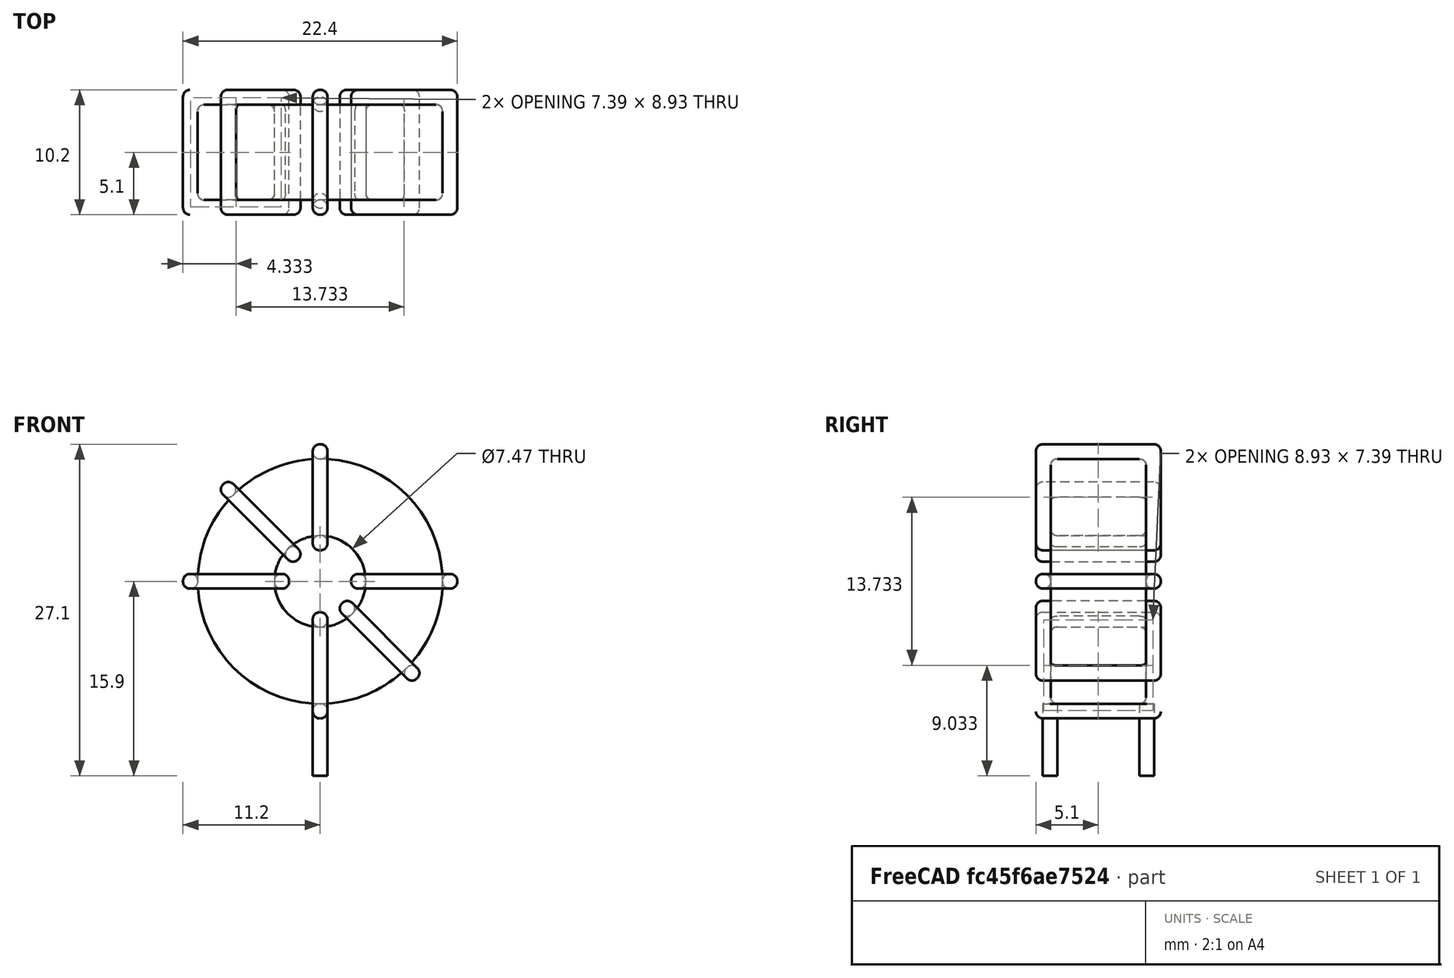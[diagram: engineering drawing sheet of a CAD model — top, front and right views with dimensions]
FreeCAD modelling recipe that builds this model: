
FCSTD DOCUMENT  (FreeCAD 0.16R6703 (Git))
Label: L_Toroid_Vertical_L22.4mm_W10.2mm_P7.90mm_Vishay_TJ4
License: All rights reserved
LicenseURL: http://en.wikipedia.org/wiki/All_rights_reserved
objects: Sketcher::SketchObject×6, PartDesign::Pad×6, PartDesign::Fillet×5, Spreadsheet::Sheet×1
note: 23 computed .brp shape members not serialized (recipe doc carries the construction recipe); baked Part::Feature solids carry a one-line shape summary decoded from their .brp

FEATURE [Spreadsheet::Sheet] Spreadsheet  label="dimensions"
  cells = A1=Wx; B1(Wx)=22.4; C1(WW)=7.466666666666666; D1=22.4; A2=Wy; B2(Wy)=10.2; D2=10.2; A3=RM; B3(RMx)=7.9; C3(RMy)=0; A4=d_wire; B4(d_wire)=1.2; A5=H; B5(H)=22.4; A6=offsetx; B6(offsetx)=11.2
FEATURE [Sketcher::SketchObject] Sketch
  Placement = pos=(0,-3.95,0) rot=(1,0,0;1.5708rad)
  expr: Placement.Base.y = -Spreadsheet.RMx / 2
  expr: Constraints[0] = Spreadsheet.Wx / 2 - Spreadsheet.d_wire
  expr: Constraints[4] = Spreadsheet.WW / 2
  expr: Constraints[2] = Spreadsheet.Wx / 2 + Spreadsheet.d_wire + 0.5
  sketch-geometry (2):
    g0: Circle CenterX=0 CenterY=12.9 CenterZ=0 NormalX=0 NormalY=0 NormalZ=1 Radius=10
    g1: Circle CenterX=0 CenterY=12.9 CenterZ=0 NormalX=0 NormalY=0 NormalZ=1 Radius=3.73333
  constraints (5):
    c: Radius(g0) = 10
    c: DistanceX(g-1,g0) = 0
    c: DistanceY(g-1,g0) = 12.9
    c: Coincident(g1,g0)
    c: Radius(g1) = 3.73333
FEATURE [PartDesign::Pad] Pad
  Length = 7.8
  Length2 = 100
  Midplane = true
  Placement = pos=(0,-3.95,0) rot=(1,0,0;1.5708rad)
  Sketch = -> Sketch
  Type = 0
  expr: Length = Spreadsheet.Wy - 2 * Spreadsheet.d_wire
FEATURE [Sketcher::SketchObject] Sketch001
  Placement = pos=(0,0,1.7) rot=(0,0,1;0rad)
  expr: Placement.Base.z = 0.5 + Spreadsheet.d_wire
  expr: Constraints[4] = Spreadsheet.RMy
  expr: Constraints[2] = -Spreadsheet.RMx
  expr: Constraints[1] = Spreadsheet.d_wire / 2
  sketch-geometry (2):
    g0: Circle CenterX=0 CenterY=0 CenterZ=0 NormalX=0 NormalY=0 NormalZ=1 Radius=0.6
    g1: Circle CenterX=0 CenterY=-7.9 CenterZ=0 NormalX=0 NormalY=0 NormalZ=1 Radius=0.6
  constraints (5):
    c: Equal(g0,g1)
    c: Radius(g0) = 0.6
    c: DistanceY(g-1,g1) = -7.9
    c: Coincident(g0,g-1)
    c: DistanceX(g-1,g1) = 0
FEATURE [PartDesign::Pad] Pad001
  Length = 1.2
  Length2 = 4.7
  Placement = pos=(0,0,1.7) rot=(0,0,1;0rad)
  Reversed = true
  Sketch = -> Sketch001
  Type = 4
  expr: Length2 = 3.5 + Spreadsheet.d_wire
  expr: Length = Spreadsheet.d_wire
FEATURE [PartDesign::Fillet] Fillet
  Base = -> Pad [Edge6,Edge3,Edge2]
  Placement = pos=(0,-3.95,0) rot=(1,0,0;1.5708rad)
  Radius = 0.5
FEATURE [Sketcher::SketchObject] Sketch003
  Placement = pos=(0,1.15,12.9) rot=(1,0,0;3.14159rad)
  expr: Constraints[18] = Spreadsheet.d_wire
  expr: Constraints[16] = Spreadsheet.d_wire
  expr: Constraints[19] = Spreadsheet.d_wire
  expr: Constraints[17] = Spreadsheet.d_wire
  expr: Placement.Base.y = -1 * (Spreadsheet.RMx - Spreadsheet.Wy) / 2
  expr: Constraints[21] = (Spreadsheet.Wx - Spreadsheet.WW) / 2 - Spreadsheet.d_wire
  expr: Constraints[22] = Spreadsheet.Wx / 2 - Spreadsheet.d_wire
  expr: Constraints[43] = Spreadsheet.d_wire
  expr: Constraints[48] = Spreadsheet.Wx - Spreadsheet.d_wire * 2
  expr: Constraints[49] = Spreadsheet.Wy
  expr: Placement.Base.z = Spreadsheet.Wx / 2 + Spreadsheet.d_wire + 0.5
  sketch-geometry (16):
    g0: LineSegment StartX=-2.53333 StartY=0 StartZ=0 EndX=-11.2 EndY=0 EndZ=0
    g1: LineSegment StartX=-11.2 StartY=0 StartZ=0 EndX=-11.2 EndY=10.2 EndZ=0
    g2: LineSegment StartX=-11.2 StartY=10.2 StartZ=0 EndX=-2.53333 EndY=10.2 EndZ=0
    g3: LineSegment StartX=-2.53333 StartY=10.2 StartZ=0 EndX=-2.53333 EndY=0 EndZ=0
    g4: LineSegment StartX=-10 StartY=9 StartZ=0 EndX=-3.73333 EndY=9 EndZ=0
    g5: LineSegment StartX=-3.73333 StartY=9 StartZ=0 EndX=-3.73333 EndY=1.2 EndZ=0
    g6: LineSegment StartX=-3.73333 StartY=1.2 StartZ=0 EndX=-10 EndY=1.2 EndZ=0
    g7: LineSegment StartX=-10 StartY=1.2 StartZ=0 EndX=-10 EndY=9 EndZ=0
    g8: LineSegment StartX=2.53333 StartY=10.2 StartZ=0 EndX=11.2 EndY=10.2 EndZ=0
    g9: LineSegment StartX=11.2 StartY=10.2 StartZ=0 EndX=11.2 EndY=0 EndZ=0
    g10: LineSegment StartX=11.2 StartY=0 StartZ=0 EndX=2.53333 EndY=0 EndZ=0
    g11: LineSegment StartX=2.53333 StartY=0 StartZ=0 EndX=2.53333 EndY=10.2 EndZ=0
    g12: LineSegment StartX=3.73333 StartY=9 StartZ=0 EndX=10 EndY=9 EndZ=0
    g13: LineSegment StartX=10 StartY=9 StartZ=0 EndX=10 EndY=1.2 EndZ=0
    g14: LineSegment StartX=10 StartY=1.2 StartZ=0 EndX=3.73333 EndY=1.2 EndZ=0
    g15: LineSegment StartX=3.73333 StartY=1.2 StartZ=0 EndX=3.73333 EndY=9 EndZ=0
  constraints (50):
    c: Horizontal(g0)
    c: Coincident(g1,g0)
    c: Vertical(g1)
    c: Coincident(g2,g1)
    c: Horizontal(g2)
    c: Coincident(g3,g2)
    c: Coincident(g3,g0)
    c: Vertical(g3)
    c: Coincident(g4,g5)
    c: Coincident(g5,g6)
    c: Coincident(g6,g7)
    c: Coincident(g7,g4)
    c: Horizontal(g4)
    c: Horizontal(g6)
    c: Vertical(g5)
    c: Vertical(g7)
    c: DistanceX(g1,g4) = 1.2
    c: DistanceY(g4,g1) = 1.2
    c: DistanceX(g5,g0) = 1.2
    c: DistanceY(g0,g5) = 1.2
    c: DistanceY(g-1,g0) = 0
    c: DistanceX(g6,g6) = 6.26667
    c: DistanceX(g6,g-1) = 10
    c: Coincident(g8,g9)
    c: Coincident(g9,g10)
    c: Coincident(g10,g11)
    c: Coincident(g11,g8)
    c: Horizontal(g8)
    c: Horizontal(g10)
    c: Vertical(g9)
    c: Vertical(g11)
    c: Coincident(g12,g13)
    c: Coincident(g13,g14)
    c: Coincident(g14,g15)
    c: Coincident(g15,g12)
    c: Horizontal(g12)
    c: Horizontal(g14)
    c: Vertical(g13)
    c: Vertical(g15)
    c: DistanceY(g8,g2) = 0
    c: DistanceY(g10,g0) = 0
    c: DistanceY(g14,g5) = 0
    c: DistanceY(g12,g4) = 0
    c: DistanceX(g8,g12) = 1.2
    c: Equal(g8,g2)
    c: Equal(g12,g4)
    c: Equal(g9,g1)
    c: Equal(g13,g7)
    c: DistanceX(g4,g12) = 20
    c: DistanceY(g0,g1) = 10.2
FEATURE [PartDesign::Pad] Pad002
  Length = 1.2
  Length2 = 100
  Midplane = true
  Placement = pos=(0,1.15,12.9) rot=(1,0,0;3.14159rad)
  Sketch = -> Sketch003
  Type = 0
  expr: Length = Spreadsheet.d_wire
FEATURE [PartDesign::Fillet] Fillet001
  Base = -> Pad002 [Edge38,Edge41,Edge42,Edge43,Edge29,Edge32,Edge33,Edge34,Edge25,Edge35,Edge36,Edge13,Edge14,Edge15,Edge16,Edge17,Edge18,Edge19,Edge1,Edge2,Edge3,Edge4,Edge5,Edge6,Edge7,Edge37,Edge39,Edge40,Edge20,Edge23,Edge24,Edge21,Edge22,Edge8,Edge9,Edge10,Edge11,Edge12,Edge26,Edge27,+8 more]
  Placement = pos=(0,1.15,12.9) rot=(1,0,0;3.14159rad)
  Radius = 0.564
  expr: Radius = Spreadsheet.d_wire * 0.47
FEATURE [Sketcher::SketchObject] Sketch004
  Placement = pos=(0,1.15,12.9) rot=(0.92388,0,0.382683;3.14159rad)
  expr: Constraints[18] = Spreadsheet.d_wire
  expr: Constraints[16] = Spreadsheet.d_wire
  expr: Constraints[19] = Spreadsheet.d_wire
  expr: Constraints[17] = Spreadsheet.d_wire
  expr: Placement.Base.y = -1 * (Spreadsheet.RMx - Spreadsheet.Wy) / 2
  expr: Constraints[21] = (Spreadsheet.Wx - Spreadsheet.WW) / 2 - Spreadsheet.d_wire
  expr: Constraints[22] = Spreadsheet.Wx / 2 - Spreadsheet.d_wire
  expr: Constraints[43] = Spreadsheet.d_wire
  expr: Constraints[48] = Spreadsheet.Wx - 2 * Spreadsheet.d_wire
  expr: Constraints[49] = Spreadsheet.Wy
  expr: Placement.Base.z = Spreadsheet.Wx / 2 + Spreadsheet.d_wire + 0.5
  sketch-geometry (16):
    g0: LineSegment StartX=-2.53333 StartY=0 StartZ=0 EndX=-11.2 EndY=0 EndZ=0
    g1: LineSegment StartX=-11.2 StartY=0 StartZ=0 EndX=-11.2 EndY=10.2 EndZ=0
    g2: LineSegment StartX=-11.2 StartY=10.2 StartZ=0 EndX=-2.53333 EndY=10.2 EndZ=0
    g3: LineSegment StartX=-2.53333 StartY=10.2 StartZ=0 EndX=-2.53333 EndY=0 EndZ=0
    g4: LineSegment StartX=-10 StartY=9 StartZ=0 EndX=-3.73333 EndY=9 EndZ=0
    g5: LineSegment StartX=-3.73333 StartY=9 StartZ=0 EndX=-3.73333 EndY=1.2 EndZ=0
    g6: LineSegment StartX=-3.73333 StartY=1.2 StartZ=0 EndX=-10 EndY=1.2 EndZ=0
    g7: LineSegment StartX=-10 StartY=1.2 StartZ=0 EndX=-10 EndY=9 EndZ=0
    g8: LineSegment StartX=2.53333 StartY=10.2 StartZ=0 EndX=11.2 EndY=10.2 EndZ=0
    g9: LineSegment StartX=11.2 StartY=10.2 StartZ=0 EndX=11.2 EndY=0 EndZ=0
    g10: LineSegment StartX=11.2 StartY=0 StartZ=0 EndX=2.53333 EndY=0 EndZ=0
    g11: LineSegment StartX=2.53333 StartY=0 StartZ=0 EndX=2.53333 EndY=10.2 EndZ=0
    g12: LineSegment StartX=3.73333 StartY=9 StartZ=0 EndX=10 EndY=9 EndZ=0
    g13: LineSegment StartX=10 StartY=9 StartZ=0 EndX=10 EndY=1.2 EndZ=0
    g14: LineSegment StartX=10 StartY=1.2 StartZ=0 EndX=3.73333 EndY=1.2 EndZ=0
    g15: LineSegment StartX=3.73333 StartY=1.2 StartZ=0 EndX=3.73333 EndY=9 EndZ=0
  constraints (50):
    c: Horizontal(g0)
    c: Coincident(g1,g0)
    c: Vertical(g1)
    c: Coincident(g2,g1)
    c: Horizontal(g2)
    c: Coincident(g3,g2)
    c: Coincident(g3,g0)
    c: Vertical(g3)
    c: Coincident(g4,g5)
    c: Coincident(g5,g6)
    c: Coincident(g6,g7)
    c: Coincident(g7,g4)
    c: Horizontal(g4)
    c: Horizontal(g6)
    c: Vertical(g5)
    c: Vertical(g7)
    c: DistanceX(g1,g4) = 1.2
    c: DistanceY(g4,g1) = 1.2
    c: DistanceX(g5,g0) = 1.2
    c: DistanceY(g0,g5) = 1.2
    c: DistanceY(g-1,g0) = 0
    c: DistanceX(g6,g6) = 6.26667
    c: DistanceX(g6,g-1) = 10
    c: Coincident(g8,g9)
    c: Coincident(g9,g10)
    c: Coincident(g10,g11)
    c: Coincident(g11,g8)
    c: Horizontal(g8)
    c: Horizontal(g10)
    c: Vertical(g9)
    c: Vertical(g11)
    c: Coincident(g12,g13)
    c: Coincident(g13,g14)
    c: Coincident(g14,g15)
    c: Coincident(g15,g12)
    c: Horizontal(g12)
    c: Horizontal(g14)
    c: Vertical(g13)
    c: Vertical(g15)
    c: DistanceY(g8,g2) = 0
    c: DistanceY(g10,g0) = 0
    c: DistanceY(g14,g5) = 0
    c: DistanceY(g12,g4) = 0
    c: DistanceX(g8,g12) = 1.2
    c: Equal(g8,g2)
    c: Equal(g12,g4)
    c: Equal(g9,g1)
    c: Equal(g13,g7)
    c: DistanceX(g4,g12) = 20
    c: DistanceY(g0,g1) = 10.2
FEATURE [PartDesign::Pad] Pad003
  Length = 1.2
  Length2 = 100
  Midplane = true
  Placement = pos=(0,1.15,12.9) rot=(0.92388,0,0.382683;3.14159rad)
  Sketch = -> Sketch004
  Type = 0
  expr: Length = Spreadsheet.d_wire
FEATURE [PartDesign::Fillet] Fillet002
  Base = -> Pad003 [Edge38,Edge41,Edge42,Edge43,Edge29,Edge32,Edge33,Edge34,Edge25,Edge35,Edge36,Edge13,Edge14,Edge15,Edge16,Edge17,Edge18,Edge19,Edge1,Edge2,Edge3,Edge4,Edge5,Edge6,Edge7,Edge37,Edge39,Edge40,Edge20,Edge23,Edge24,Edge21,Edge22,Edge8,Edge9,Edge10,Edge11,Edge12,Edge26,Edge27,+8 more]
  Placement = pos=(0,1.15,12.9) rot=(0.92388,0,0.382683;3.14159rad)
  Radius = 0.564
  expr: Radius = Spreadsheet.d_wire * 0.47
FEATURE [Sketcher::SketchObject] Sketch005
  Placement = pos=(0,1.15,12.9) rot=(0.92388,0,-0.382683;3.14159rad)
  expr: Constraints[18] = Spreadsheet.d_wire
  expr: Constraints[16] = Spreadsheet.d_wire
  expr: Constraints[19] = Spreadsheet.d_wire
  expr: Constraints[17] = Spreadsheet.d_wire
  expr: Placement.Base.y = -1 * (Spreadsheet.RMx - Spreadsheet.Wy) / 2
  expr: Constraints[21] = (Spreadsheet.Wx - Spreadsheet.WW) / 2 - Spreadsheet.d_wire
  expr: Constraints[22] = Spreadsheet.Wx / 2 - Spreadsheet.d_wire
  expr: Constraints[43] = Spreadsheet.d_wire
  expr: Constraints[48] = Spreadsheet.Wx - 2 * Spreadsheet.d_wire
  expr: Constraints[49] = Spreadsheet.Wy
  expr: Placement.Base.z = Spreadsheet.Wx / 2 + Spreadsheet.d_wire + 0.5
  sketch-geometry (16):
    g0: LineSegment StartX=-2.53333 StartY=0 StartZ=0 EndX=-11.2 EndY=0 EndZ=0
    g1: LineSegment StartX=-11.2 StartY=0 StartZ=0 EndX=-11.2 EndY=10.2 EndZ=0
    g2: LineSegment StartX=-11.2 StartY=10.2 StartZ=0 EndX=-2.53333 EndY=10.2 EndZ=0
    g3: LineSegment StartX=-2.53333 StartY=10.2 StartZ=0 EndX=-2.53333 EndY=0 EndZ=0
    g4: LineSegment StartX=-10 StartY=9 StartZ=0 EndX=-3.73333 EndY=9 EndZ=0
    g5: LineSegment StartX=-3.73333 StartY=9 StartZ=0 EndX=-3.73333 EndY=1.2 EndZ=0
    g6: LineSegment StartX=-3.73333 StartY=1.2 StartZ=0 EndX=-10 EndY=1.2 EndZ=0
    g7: LineSegment StartX=-10 StartY=1.2 StartZ=0 EndX=-10 EndY=9 EndZ=0
    g8: LineSegment StartX=2.53333 StartY=10.2 StartZ=0 EndX=11.2 EndY=10.2 EndZ=0
    g9: LineSegment StartX=11.2 StartY=10.2 StartZ=0 EndX=11.2 EndY=0 EndZ=0
    g10: LineSegment StartX=11.2 StartY=0 StartZ=0 EndX=2.53333 EndY=0 EndZ=0
    g11: LineSegment StartX=2.53333 StartY=0 StartZ=0 EndX=2.53333 EndY=10.2 EndZ=0
    g12: LineSegment StartX=3.73333 StartY=9 StartZ=0 EndX=10 EndY=9 EndZ=0
    g13: LineSegment StartX=10 StartY=9 StartZ=0 EndX=10 EndY=1.2 EndZ=0
    g14: LineSegment StartX=10 StartY=1.2 StartZ=0 EndX=3.73333 EndY=1.2 EndZ=0
    g15: LineSegment StartX=3.73333 StartY=1.2 StartZ=0 EndX=3.73333 EndY=9 EndZ=0
  constraints (50):
    c: Horizontal(g0)
    c: Coincident(g1,g0)
    c: Vertical(g1)
    c: Coincident(g2,g1)
    c: Horizontal(g2)
    c: Coincident(g3,g2)
    c: Coincident(g3,g0)
    c: Vertical(g3)
    c: Coincident(g4,g5)
    c: Coincident(g5,g6)
    c: Coincident(g6,g7)
    c: Coincident(g7,g4)
    c: Horizontal(g4)
    c: Horizontal(g6)
    c: Vertical(g5)
    c: Vertical(g7)
    c: DistanceX(g1,g4) = 1.2
    c: DistanceY(g4,g1) = 1.2
    c: DistanceX(g5,g0) = 1.2
    c: DistanceY(g0,g5) = 1.2
    c: DistanceY(g-1,g0) = 0
    c: DistanceX(g6,g6) = 6.26667
    c: DistanceX(g6,g-1) = 10
    c: Coincident(g8,g9)
    c: Coincident(g9,g10)
    c: Coincident(g10,g11)
    c: Coincident(g11,g8)
    c: Horizontal(g8)
    c: Horizontal(g10)
    c: Vertical(g9)
    c: Vertical(g11)
    c: Coincident(g12,g13)
    c: Coincident(g13,g14)
    c: Coincident(g14,g15)
    c: Coincident(g15,g12)
    c: Horizontal(g12)
    c: Horizontal(g14)
    c: Vertical(g13)
    c: Vertical(g15)
    c: DistanceY(g8,g2) = 0
    c: DistanceY(g10,g0) = 0
    c: DistanceY(g14,g5) = 0
    c: DistanceY(g12,g4) = 0
    c: DistanceX(g8,g12) = 1.2
    c: Equal(g8,g2)
    c: Equal(g12,g4)
    c: Equal(g9,g1)
    c: Equal(g13,g7)
    c: DistanceX(g4,g12) = 20
    c: DistanceY(g0,g1) = 10.2
FEATURE [PartDesign::Pad] Pad004
  Length = 1.2
  Length2 = 100
  Midplane = true
  Placement = pos=(0,1.15,12.9) rot=(0.92388,0,-0.382683;3.14159rad)
  Sketch = -> Sketch005
  Type = 0
  expr: Length = Spreadsheet.d_wire
FEATURE [PartDesign::Fillet] Fillet003
  Base = -> Pad004 [Edge38,Edge41,Edge42,Edge43,Edge29,Edge32,Edge33,Edge34,Edge25,Edge35,Edge36,Edge13,Edge14,Edge15,Edge16,Edge17,Edge18,Edge19,Edge1,Edge2,Edge3,Edge4,Edge5,Edge6,Edge7,Edge37,Edge39,Edge40,Edge20,Edge23,Edge24,Edge21,Edge22,Edge8,Edge9,Edge10,Edge11,Edge12,Edge26,Edge27,+8 more]
  Placement = pos=(0,1.15,12.9) rot=(0.92388,0,-0.382683;3.14159rad)
  Radius = 0.564
  expr: Radius = Spreadsheet.d_wire * 0.47
FEATURE [Sketcher::SketchObject] Sketch006
  Placement = pos=(0,1.15,12.9) rot=(0.707107,0,0.707107;3.14159rad)
  expr: Constraints[18] = Spreadsheet.d_wire
  expr: Constraints[16] = Spreadsheet.d_wire
  expr: Constraints[19] = Spreadsheet.d_wire
  expr: Constraints[17] = Spreadsheet.d_wire
  expr: Placement.Base.y = -1 * (Spreadsheet.RMx - Spreadsheet.Wy) / 2
  expr: Constraints[21] = (Spreadsheet.Wx - Spreadsheet.WW) / 2 - Spreadsheet.d_wire
  expr: Constraints[22] = Spreadsheet.Wx / 2 - Spreadsheet.d_wire
  expr: Constraints[43] = Spreadsheet.d_wire
  expr: Constraints[48] = Spreadsheet.Wx - Spreadsheet.d_wire * 2
  expr: Constraints[49] = Spreadsheet.Wy
  expr: Placement.Base.z = Spreadsheet.Wx / 2 + Spreadsheet.d_wire + 0.5
  sketch-geometry (16):
    g0: LineSegment StartX=-2.53333 StartY=0 StartZ=0 EndX=-11.2 EndY=0 EndZ=0
    g1: LineSegment StartX=-11.2 StartY=0 StartZ=0 EndX=-11.2 EndY=10.2 EndZ=0
    g2: LineSegment StartX=-11.2 StartY=10.2 StartZ=0 EndX=-2.53333 EndY=10.2 EndZ=0
    g3: LineSegment StartX=-2.53333 StartY=10.2 StartZ=0 EndX=-2.53333 EndY=0 EndZ=0
    g4: LineSegment StartX=-10 StartY=9 StartZ=0 EndX=-3.73333 EndY=9 EndZ=0
    g5: LineSegment StartX=-3.73333 StartY=9 StartZ=0 EndX=-3.73333 EndY=1.2 EndZ=0
    g6: LineSegment StartX=-3.73333 StartY=1.2 StartZ=0 EndX=-10 EndY=1.2 EndZ=0
    g7: LineSegment StartX=-10 StartY=1.2 StartZ=0 EndX=-10 EndY=9 EndZ=0
    g8: LineSegment StartX=2.53333 StartY=10.2 StartZ=0 EndX=11.2 EndY=10.2 EndZ=0
    g9: LineSegment StartX=11.2 StartY=10.2 StartZ=0 EndX=11.2 EndY=0 EndZ=0
    g10: LineSegment StartX=11.2 StartY=0 StartZ=0 EndX=2.53333 EndY=0 EndZ=0
    g11: LineSegment StartX=2.53333 StartY=0 StartZ=0 EndX=2.53333 EndY=10.2 EndZ=0
    g12: LineSegment StartX=3.73333 StartY=9 StartZ=0 EndX=10 EndY=9 EndZ=0
    g13: LineSegment StartX=10 StartY=9 StartZ=0 EndX=10 EndY=1.2 EndZ=0
    g14: LineSegment StartX=10 StartY=1.2 StartZ=0 EndX=3.73333 EndY=1.2 EndZ=0
    g15: LineSegment StartX=3.73333 StartY=1.2 StartZ=0 EndX=3.73333 EndY=9 EndZ=0
  constraints (50):
    c: Horizontal(g0)
    c: Coincident(g1,g0)
    c: Vertical(g1)
    c: Coincident(g2,g1)
    c: Horizontal(g2)
    c: Coincident(g3,g2)
    c: Coincident(g3,g0)
    c: Vertical(g3)
    c: Coincident(g4,g5)
    c: Coincident(g5,g6)
    c: Coincident(g6,g7)
    c: Coincident(g7,g4)
    c: Horizontal(g4)
    c: Horizontal(g6)
    c: Vertical(g5)
    c: Vertical(g7)
    c: DistanceX(g1,g4) = 1.2
    c: DistanceY(g4,g1) = 1.2
    c: DistanceX(g5,g0) = 1.2
    c: DistanceY(g0,g5) = 1.2
    c: DistanceY(g-1,g0) = 0
    c: DistanceX(g6,g6) = 6.26667
    c: DistanceX(g6,g-1) = 10
    c: Coincident(g8,g9)
    c: Coincident(g9,g10)
    c: Coincident(g10,g11)
    c: Coincident(g11,g8)
    c: Horizontal(g8)
    c: Horizontal(g10)
    c: Vertical(g9)
    c: Vertical(g11)
    c: Coincident(g12,g13)
    c: Coincident(g13,g14)
    c: Coincident(g14,g15)
    c: Coincident(g15,g12)
    c: Horizontal(g12)
    c: Horizontal(g14)
    c: Vertical(g13)
    c: Vertical(g15)
    c: DistanceY(g8,g2) = 0
    c: DistanceY(g10,g0) = 0
    c: DistanceY(g14,g5) = 0
    c: DistanceY(g12,g4) = 0
    c: DistanceX(g8,g12) = 1.2
    c: Equal(g8,g2)
    c: Equal(g12,g4)
    c: Equal(g9,g1)
    c: Equal(g13,g7)
    c: DistanceX(g4,g12) = 20
    c: DistanceY(g0,g1) = 10.2
FEATURE [PartDesign::Pad] Pad005
  Length = 1.2
  Length2 = 100
  Midplane = true
  Placement = pos=(0,1.15,12.9) rot=(0.707107,0,0.707107;3.14159rad)
  Sketch = -> Sketch006
  Type = 0
  expr: Length = Spreadsheet.d_wire
FEATURE [PartDesign::Fillet] Fillet004
  Base = -> Pad005 [Edge38,Edge41,Edge42,Edge43,Edge29,Edge32,Edge33,Edge34,Edge25,Edge35,Edge36,Edge13,Edge14,Edge15,Edge16,Edge17,Edge18,Edge19,Edge1,Edge2,Edge3,Edge4,Edge5,Edge6,Edge7,Edge37,Edge39,Edge40,Edge20,Edge23,Edge24,Edge21,Edge22,Edge8,Edge9,Edge10,Edge11,Edge12,Edge26,Edge27,+8 more]
  Placement = pos=(0,1.15,12.9) rot=(0.707107,0,0.707107;3.14159rad)
  Radius = 0.564
  expr: Radius = Spreadsheet.d_wire * 0.47
